# Revit family: KEUCO_59556000170_
name_source: partatom
category: Generic Models
revit_build: Autodesk Revit 2016 (Build: 20150220_1215(x64)
units: mm (PartAtom-declared; Revit-internal decimal feet)

## family parameters
Always vertical = No
Can host rebar = No
Cut with Voids When Loaded = No
Part Type = Normal
Room Calculation Point = No
Round Connector Dimension = Use Diameter
Shared = No
Work Plane-Based = Yes

## types (1)
- 59556000170
    Artikelnummer = 59556000170
    Ausschreibungstext = KEUCO IXMO UP Funktionseinheit für 2-Wege Umstellventil 
mit Schlauchanschluss DN15, 59556000170
schallentkoppelter Grundkörper aus entzinkungsarmen Messing
für den Wandeinbau, frei positionierbar,
eigensicher gegen Rückfließen, Einbautiefe 80 – 110 mm,
Grundplatte mit Einstellschrauben zur optimalen Ausrichtung,
Anschlüsse G 1/2 Zoll mit farblicher Kennzeichnung
Hinweis: passend zu Artikel-Nr. 
59556010101, 59556010102, 59556010201
59556010202, 59557010101, 59557010102
59557010201, 59557010202, 59556011101
59556011102, 59556011201, 59556011202
59557011101, 59557011102, 59557011201
59557011202
    Breite = 45 mm  [stored 0.147638 ft]
    Default Elevation = 1219 mm
    Description = Grundkörper für Wandeinbau,
Einbautiefe 80 - 110 mm
    Gewicht = 0
    Kategorie = ARM
ARM
ARM
    Manufacturer = KEUCO
    Material = Stahl, verchromt
    Serie = Plan
    URL = https://www.keuco.com
    Verwendung = DU / WA / ZU

note: [stored X ft] marks values corroborated as IEEE doubles in the binary element streams (Revit-internal decimal feet)

## geometry (parser evidence)
native form markers: Sweep x3
no freeform markers — native parametric forms only
